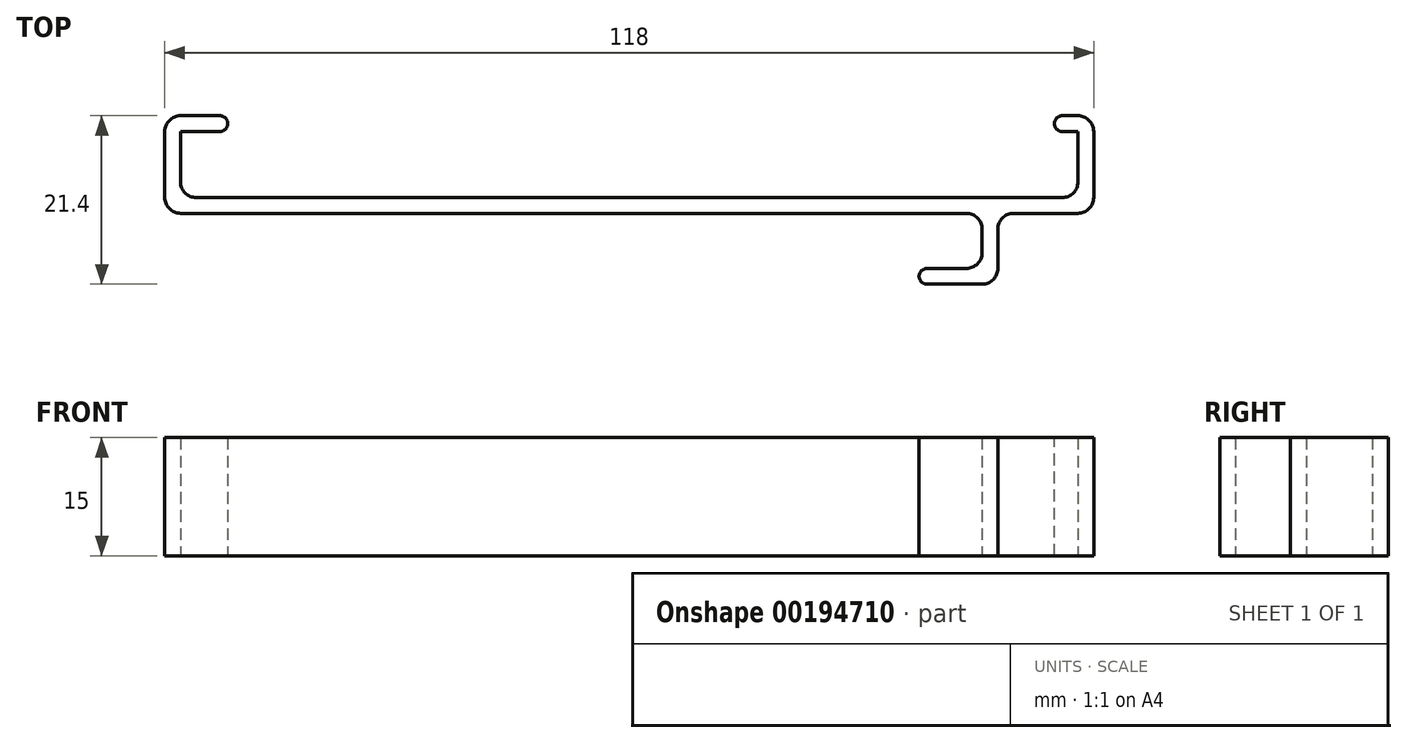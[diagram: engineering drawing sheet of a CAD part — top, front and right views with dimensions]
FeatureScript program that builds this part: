
annotation { "Feature Type Name" : "Feature", "Feature Type Description" : "" }
export const myFeature = defineFeature(function(context is Context, id is Id, definition is map)
    precondition{}
    {
        {
            var Q0;
            Q0=qCreatedBy(makeId("Top.planeOp"),FACE);
            var sketch = newSketch(context, id + "F0", { "sketchPlane" : qUnion([Q0])});
            skLineSegment(sketch, "E0.bottom", {"start": v(-52.45, -0.07) * mm, "end": v(61.55, -0.07) * mm});
            skLineSegment(sketch, "E0.top", {"start": v(-52.45, -2.07) * mm, "end": v(61.55, -2.07) * mm});
            skLineSegment(sketch, "E0.left", {"start": v(-52.45, -0.07) * mm, "end": v(-52.45, -2.07) * mm});
            skLineSegment(sketch, "E0.right", {"start": v(61.55, -0.07) * mm, "end": v(61.55, -2.07) * mm});
            skLineSegment(sketch, "E1.bottom", {"start": v(-52.45, -2.07) * mm, "end": v(-54.45, -2.07) * mm});
            skLineSegment(sketch, "E1.top", {"start": v(-52.45, 8.33) * mm, "end": v(-54.45, 8.33) * mm});
            skLineSegment(sketch, "E1.left", {"start": v(-52.45, -2.07) * mm, "end": v(-52.45, 8.33) * mm});
            skLineSegment(sketch, "E1.right", {"start": v(-54.45, -2.07) * mm, "end": v(-54.45, 8.33) * mm});
            skLineSegment(sketch, "E2.bottom", {"start": v(61.55, -2.07) * mm, "end": v(63.55, -2.07) * mm});
            skLineSegment(sketch, "E2.top", {"start": v(61.55, 8.33) * mm, "end": v(63.55, 8.33) * mm});
            skLineSegment(sketch, "E2.left", {"start": v(61.55, -2.07) * mm, "end": v(61.55, 8.33) * mm});
            skLineSegment(sketch, "E2.right", {"start": v(63.55, -2.07) * mm, "end": v(63.55, 8.33) * mm});
            skLineSegment(sketch, "E3.bottom", {"start": v(-54.45, 8.33) * mm, "end": v(-46.45, 8.33) * mm});
            skLineSegment(sketch, "E3.top", {"start": v(-54.45, 10.33) * mm, "end": v(-46.45, 10.33) * mm});
            skLineSegment(sketch, "E3.left", {"start": v(-54.45, 8.33) * mm, "end": v(-54.45, 10.33) * mm});
            skLineSegment(sketch, "E3.right", {"start": v(-46.45, 8.33) * mm, "end": v(-46.45, 10.33) * mm});
            skLineSegment(sketch, "E4.bottom", {"start": v(63.55, 8.33) * mm, "end": v(58.55, 8.33) * mm});
            skLineSegment(sketch, "E4.top", {"start": v(63.55, 10.33) * mm, "end": v(58.55, 10.33) * mm});
            skLineSegment(sketch, "E4.left", {"start": v(63.55, 8.33) * mm, "end": v(63.55, 10.33) * mm});
            skLineSegment(sketch, "E4.right", {"start": v(58.55, 8.33) * mm, "end": v(58.55, 10.33) * mm});
            skLineSegment(sketch, "E5.bottom", {"start": v(51.37, -2.07) * mm, "end": v(49.37, -2.07) * mm});
            skLineSegment(sketch, "E5.top", {"start": v(51.37, -9.07) * mm, "end": v(49.37, -9.07) * mm});
            skLineSegment(sketch, "E5.left", {"start": v(51.37, -2.07) * mm, "end": v(51.37, -9.07) * mm});
            skLineSegment(sketch, "E5.right", {"start": v(49.37, -2.07) * mm, "end": v(49.37, -9.07) * mm});
            skLineSegment(sketch, "E6.bottom", {"start": v(51.37, -9.07) * mm, "end": v(41.37, -9.07) * mm});
            skLineSegment(sketch, "E6.top", {"start": v(51.37, -11.07) * mm, "end": v(41.37, -11.07) * mm});
            skLineSegment(sketch, "E6.left", {"start": v(51.37, -9.07) * mm, "end": v(51.37, -11.07) * mm});
            skLineSegment(sketch, "E6.right", {"start": v(41.37, -9.07) * mm, "end": v(41.37, -11.07) * mm});
            skSolve(sketch);
        }
        {
            var Q0;
            Q0 = qSketchRegion(id + "F0", true);
            extrude(context, id + "F1", {"entities" : qUnion([Q0]), "depth" : 15 * mm});
        }
        {
            var Q0;
            Q0=makeQuery(id+"F1.opExtrude","SWEPT_EDGE",EDGE,{"disambiguationData":[OSD([sQuery(id+"F0.wireOp",EDGE,"E4.top"),sQuery(id+"F0.wireOp",EDGE,"E4.right")])]});
            var Q1;
            Q1=makeQuery(id+"F1.opExtrude","SWEPT_EDGE",EDGE,{"disambiguationData":[OSD([sQuery(id+"F0.wireOp",EDGE,"E4.bottom"),sQuery(id+"F0.wireOp",EDGE,"E4.right")])]});
            var Q2;
            Q2=makeQuery(id+"F1.opExtrude","SWEPT_EDGE",EDGE,{"disambiguationData":[OSD([sQuery(id+"F0.wireOp",EDGE,"E3.bottom"),sQuery(id+"F0.wireOp",EDGE,"E3.right")])]});
            var Q3;
            Q3=makeQuery(id+"F1.opExtrude","SWEPT_EDGE",EDGE,{"disambiguationData":[OSD([sQuery(id+"F0.wireOp",EDGE,"E3.top"),sQuery(id+"F0.wireOp",EDGE,"E3.right")])]});
            var Q4;
            Q4=makeQuery(id+"F1.opExtrude","SWEPT_EDGE",EDGE,{"disambiguationData":[OSD([sQuery(id+"F0.wireOp",EDGE,"E6.bottom"),sQuery(id+"F0.wireOp",EDGE,"E6.right")])]});
            var Q5;
            Q5=makeQuery(id+"F1.opExtrude","SWEPT_EDGE",EDGE,{"disambiguationData":[OSD([sQuery(id+"F0.wireOp",EDGE,"E6.top"),sQuery(id+"F0.wireOp",EDGE,"E6.right")])]});
            fillet(context, id + "F2", {"entities" : qUnion([Q0, Q1, Q2, Q3, Q4, Q5]), "radius" : 1 * mm, "tangentPropagation" : true, "allowEdgeOverflow" : false});
        }
        {
            var Q0;
            Q0=makeQuery(id+"F1.opExtrude","SWEPT_EDGE",EDGE,{"disambiguationData":[OSD([sQuery(id+"F0.wireOp",EDGE,"E3.top"),sQuery(id+"F0.wireOp",EDGE,"E3.left")])]});
            var Q1;
            Q1=makeQuery(id+"F1.opExtrude","SWEPT_EDGE",EDGE,{"disambiguationData":[OSD([sQuery(id+"F0.wireOp",EDGE,"E1.bottom"),sQuery(id+"F0.wireOp",EDGE,"E1.right")])]});
            var Q2;
            Q2=makeQuery(id+"F1.opExtrude","SWEPT_EDGE",EDGE,{"disambiguationData":[OSD([sQuery(id+"F0.wireOp",EDGE,"E2.bottom"),sQuery(id+"F0.wireOp",EDGE,"E2.right")])]});
            var Q3;
            Q3=makeQuery(id+"F1.opExtrude","SWEPT_EDGE",EDGE,{"disambiguationData":[OSD([sQuery(id+"F0.wireOp",EDGE,"E4.top"),sQuery(id+"F0.wireOp",EDGE,"E4.left")])]});
            var Q4;
            Q4=makeQuery(id+"F1.opExtrude","SWEPT_EDGE",EDGE,{"disambiguationData":[OSD([sQuery(id+"F0.wireOp",EDGE,"E6.top"),sQuery(id+"F0.wireOp",EDGE,"E6.left")])]});
            var Q5;
            Q5=makeQuery(id+"F1.opExtrude","SWEPT_EDGE",EDGE,{"disambiguationData":[OSD([sQuery(id+"F0.wireOp",EDGE,"E0.top"),sQuery(id+"F0.wireOp",EDGE,"E5.bottom"),sQuery(id+"F0.wireOp",EDGE,"E5.right")])]});
            var Q6;
            Q6=makeQuery(id+"F1.opExtrude","SWEPT_EDGE",EDGE,{"disambiguationData":[OSD([sQuery(id+"F0.wireOp",EDGE,"E0.top"),sQuery(id+"F0.wireOp",EDGE,"E5.bottom"),sQuery(id+"F0.wireOp",EDGE,"E5.left")])]});
            var Q7;
            Q7=makeQuery(id+"F1.opExtrude","SWEPT_EDGE",EDGE,{"disambiguationData":[OSD([sQuery(id+"F0.wireOp",EDGE,"E5.right"),sQuery(id+"F0.wireOp",EDGE,"E6.bottom")])]});
            var Q8;
            Q8=makeQuery(id+"F1.opExtrude","SWEPT_EDGE",EDGE,{"disambiguationData":[OSD([sQuery(id+"F0.wireOp",EDGE,"E0.bottom"),sQuery(id+"F0.wireOp",EDGE,"E1.left")])]});
            var Q9;
            Q9=makeQuery(id+"F1.opExtrude","SWEPT_EDGE",EDGE,{"disambiguationData":[OSD([sQuery(id+"F0.wireOp",EDGE,"E0.bottom"),sQuery(id+"F0.wireOp",EDGE,"E2.left")])]});
            fillet(context, id + "F3", {"entities" : qUnion([Q0, Q1, Q2, Q3, Q4, Q5, Q6, Q7, Q8, Q9]), "radius" : 2 * mm, "tangentPropagation" : true, "allowEdgeOverflow" : false});
        }
    });
